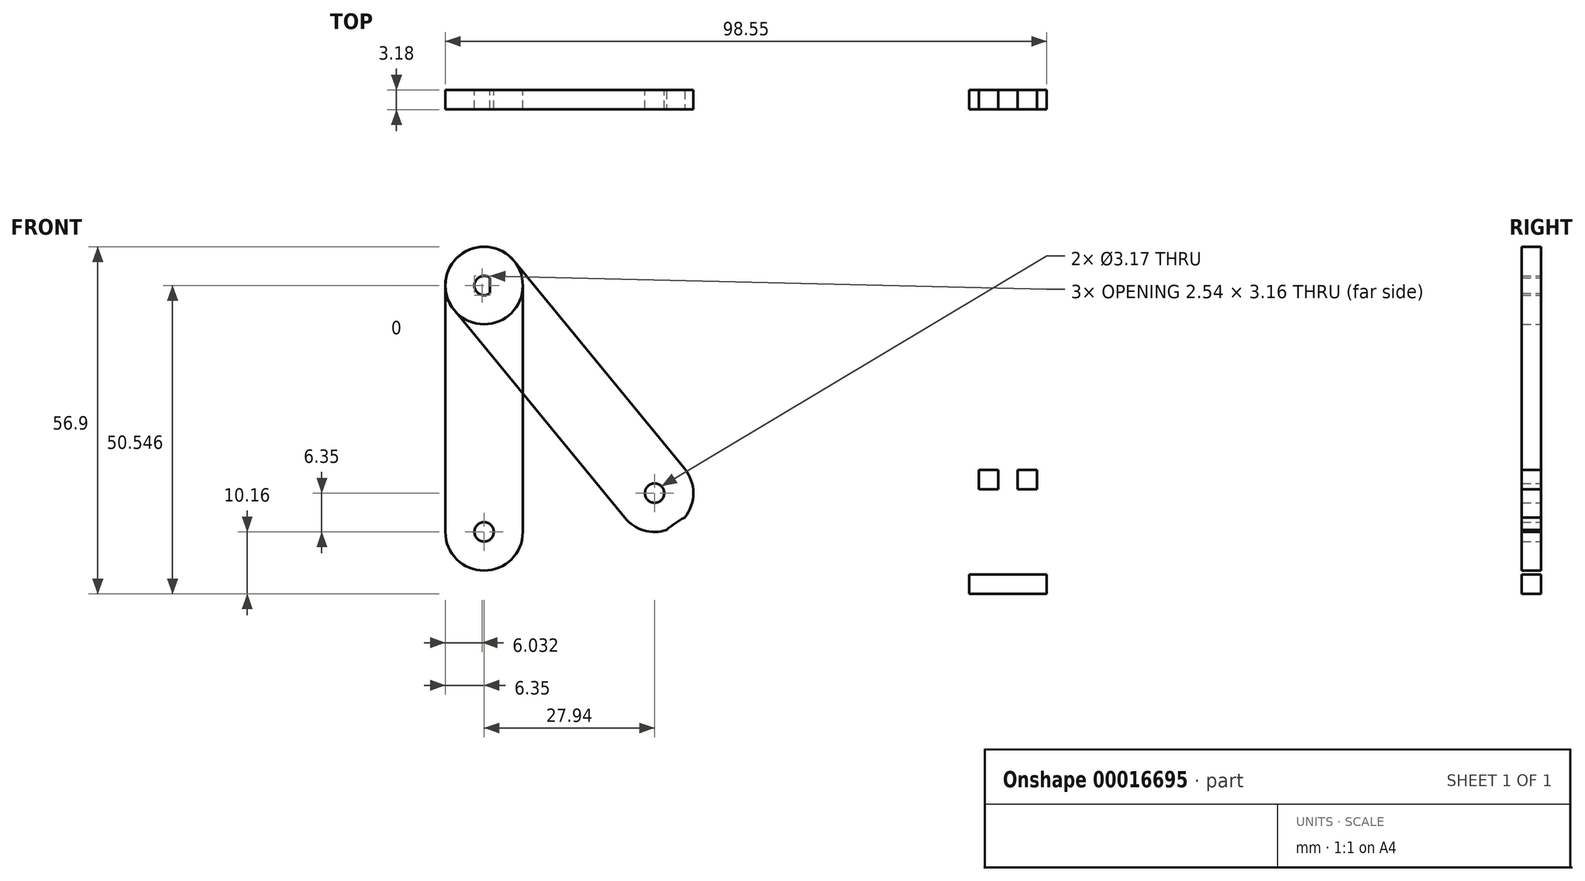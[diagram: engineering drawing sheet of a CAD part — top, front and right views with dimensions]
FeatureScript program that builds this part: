
annotation { "Feature Type Name" : "Feature", "Feature Type Description" : "" }
export const myFeature = defineFeature(function(context is Context, id is Id, definition is map)
    precondition{}
    {
        {
            var Q0;
            Q0=qCreatedBy(makeId("Front.planeOp"),FACE);
            var sketch = newSketch(context, id + "F0", { "sketchPlane" : qUnion([Q0])});
            skLineSegment(sketch, "E0.bottom", {"start": v(6.35, 0) * mm, "end": v(98.55, 0) * mm});
            skLineSegment(sketch, "E0.left", {"start": v(0, 6.35) * mm, "end": v(0, 13.97) * mm});
            skLineSegment(sketch, "E0.right", {"start": v(98.55, 0) * mm, "end": v(98.55, 20.32) * mm});
            skLineSegment(sketch, "E1.top", {"start": v(96.96, 17.15) * mm, "end": v(93.79, 17.15) * mm});
            skLineSegment(sketch, "E1.left", {"start": v(96.96, 20.32) * mm, "end": v(96.96, 17.15) * mm});
            skLineSegment(sketch, "E1.right", {"start": v(93.79, 20.32) * mm, "end": v(93.79, 17.15) * mm});
            skLineSegment(sketch, "E2.top", {"start": v(90.61, 17.15) * mm, "end": v(87.44, 17.15) * mm});
            skLineSegment(sketch, "E2.left", {"start": v(90.61, 20.32) * mm, "end": v(90.61, 17.15) * mm});
            skLineSegment(sketch, "E2.right", {"start": v(87.44, 20.32) * mm, "end": v(87.44, 17.15) * mm});
            skLineSegment(sketch, "E3.bottom", {"start": v(98.55, 20.32) * mm, "end": v(85.85, 20.32) * mm});
            skLineSegment(sketch, "E3.left", {"start": v(98.55, 20.32) * mm, "end": v(98.55, 17.15) * mm});
            skLineSegment(sketch, "E3.right", {"start": v(85.85, 20.32) * mm, "end": v(85.85, 17.15) * mm});
            skLineSegment(sketch, "E4", {"start": v(98.55, 10.16) * mm, "end": v(0, 10.16) * mm, "construction": true});
            skLineSegment(sketch, "E5", {"start": v(85.85, 20.32) * mm, "end": v(6.35, 20.32) * mm});
            skLineSegment(sketch, "E6", {"start": v(85.85, 17.15) * mm, "end": v(87.44, 17.15) * mm});
            skLineSegment(sketch, "E7", {"start": v(98.55, 17.14) * mm, "end": v(96.96, 17.14) * mm});
            skLineSegment(sketch, "E8", {"start": v(93.79, 17.15) * mm, "end": v(90.61, 17.15) * mm});
            skLineSegment(sketch, "E9.0.MirrorCS", {"start": v(85.85, 0) * mm, "end": v(85.85, 3.18) * mm});
            skLineSegment(sketch, "E10.0.MirrorCS", {"start": v(87.44, 0) * mm, "end": v(87.44, 3.18) * mm});
            skLineSegment(sketch, "E11.0.MirrorCS", {"start": v(85.85, 3.18) * mm, "end": v(87.44, 3.18) * mm});
            skLineSegment(sketch, "E12.0.MirrorCS", {"start": v(98.55, 0) * mm, "end": v(85.85, 0) * mm});
            skLineSegment(sketch, "E13.0.MirrorCS", {"start": v(90.61, 0) * mm, "end": v(90.61, 3.18) * mm});
            skLineSegment(sketch, "E14.0.MirrorCS", {"start": v(90.61, 3.18) * mm, "end": v(87.44, 3.18) * mm});
            skLineSegment(sketch, "E15.0.MirrorCS", {"start": v(93.79, 3.18) * mm, "end": v(90.61, 3.18) * mm});
            skLineSegment(sketch, "E16.0.MirrorCS", {"start": v(93.79, 0) * mm, "end": v(93.79, 3.18) * mm});
            skLineSegment(sketch, "E17.0.MirrorCS", {"start": v(96.96, 3.18) * mm, "end": v(93.79, 3.18) * mm});
            skLineSegment(sketch, "E18.0.MirrorCS", {"start": v(96.96, 0) * mm, "end": v(96.96, 3.18) * mm});
            skLineSegment(sketch, "E19.0.MirrorCS", {"start": v(98.55, 3.18) * mm, "end": v(96.96, 3.18) * mm});
            skCircle(sketch, "E20", {"center": v(34.3, 16.51) * mm, "radius": 1.59 * mm});
            skCircle(sketch, "E21", {"center": v(6.35, 10.16) * mm, "radius": 1.59 * mm});
            skPoint(sketch, "E22.visualSharp", {"position": v(0, 20.32) * mm});
            skArc(sketch, "E22.filletArc", {"start": v(6.35, 20.32) * mm, "mid": v(1.86, 18.46) * mm, "end": v(0, 13.97) * mm});
            skPoint(sketch, "E23.visualSharp", {"position": v(0, 0) * mm});
            skArc(sketch, "E23.filletArc", {"start": v(0, 6.35) * mm, "mid": v(1.86, 1.86) * mm, "end": v(6.35, 0) * mm});
            skLineSegment(sketch, "E24", {"start": v(6.35, 13.97) * mm, "end": v(6.35, 6.35) * mm, "construction": true});
            skPoint(sketch, "E25", {"position": v(92.2, 10.16) * mm});
            skPoint(sketch, "E26", {"position": v(52.07, 10.16) * mm});
            skPoint(sketch, "E27", {"position": v(6.35, 48.52) * mm});
            skLineSegment(sketch, "E28", {"start": v(6.35, 48.52) * mm, "end": v(6.35, 10.16) * mm, "construction": true});
            skLineSegment(sketch, "E29", {"start": v(6.35, 48.52) * mm, "end": v(52.07, 10.16) * mm, "construction": true});
            skSolve(sketch);
        }
        {
            var Q0;
            Q0=makeQuery(id+"F0.imprint","IMPRINT",FACE,{"disambiguationData":[TD([[makeQuery(id+"F0.imprint","IMPRINT",EDGE,{"derivedFrom":sQuery(id+"F0.wireOp",EDGE,"E0.bottom")}),1.0]])]});
            var Q1;
            Q1=makeQuery(id+"F0.imprint","IMPRINT",FACE,{"disambiguationData":[TD([[makeQuery(id+"F0.imprint","IMPRINT",EDGE,{"derivedFrom":sQuery(id+"F0.wireOp",EDGE,"E1.top")}),-1.0]])]});
            var Q2;
            Q2=makeQuery(id+"F0.imprint","IMPRINT",FACE,{"disambiguationData":[TD([[makeQuery(id+"F0.imprint","IMPRINT",EDGE,{"derivedFrom":sQuery(id+"F0.wireOp",EDGE,"E2.top")}),-1.0]])]});
            var Q3;
            {var subQ2=sQuery(id+"F0.wireOp",EDGE,"E10.0.MirrorCS");Q3=makeQuery(id+"F0.imprint","IMPRINT",FACE,{"disambiguationData":[TD([[makeQuery(id+"F0.imprint","IMPRINT",EDGE,{"derivedFrom":subQ2}),-1.0]])]});}
            var Q4;
            {var subQ1=sQuery(id+"F0.wireOp",EDGE,"E16.0.MirrorCS");Q4=makeQuery(id+"F0.imprint","IMPRINT",FACE,{"disambiguationData":[TD([[makeQuery(id+"F0.imprint","IMPRINT",EDGE,{"derivedFrom":subQ1}),-1.0]])]});}
            extrude(context, id + "F1", {"entities" : qUnion([Q0, Q1, Q2, Q3, Q4]), "depth" : 3.17 * mm});
        }
        {
            var Q0;
            Q0=qCreatedBy(makeId("Front.planeOp"),FACE);
            var sketch = newSketch(context, id + "F2", { "sketchPlane" : qUnion([Q0])});
            skCircle(sketch, "E30.0", {"center": v(6.35, 10.16) * mm, "radius": 1.59 * mm});
            skLineSegment(sketch, "E31.bottom", {"start": v(6.35, 3.81) * mm, "end": v(6.35, 3.81) * mm});
            skLineSegment(sketch, "E31.top", {"start": v(6.35, 56.9) * mm, "end": v(6.35, 56.9) * mm});
            skLineSegment(sketch, "E31.left", {"start": v(0, 10.16) * mm, "end": v(0, 50.55) * mm});
            skLineSegment(sketch, "E31.right", {"start": v(12.7, 10.16) * mm, "end": v(12.7, 50.55) * mm});
            skPoint(sketch, "E32.visualSharp", {"position": v(12.7, 3.81) * mm});
            skArc(sketch, "E32.filletArc", {"start": v(6.35, 3.81) * mm, "mid": v(10.84, 5.67) * mm, "end": v(12.7, 10.16) * mm});
            skPoint(sketch, "E33.visualSharp", {"position": v(0, 3.81) * mm});
            skArc(sketch, "E33.filletArc", {"start": v(0, 10.16) * mm, "mid": v(1.86, 5.67) * mm, "end": v(6.35, 3.81) * mm});
            skPoint(sketch, "E34.visualSharp", {"position": v(12.7, 56.9) * mm});
            skArc(sketch, "E34.filletArc", {"start": v(12.7, 50.55) * mm, "mid": v(10.84, 55.04) * mm, "end": v(6.35, 56.9) * mm});
            skPoint(sketch, "E35.visualSharp", {"position": v(0, 56.9) * mm});
            skArc(sketch, "E35.filletArc", {"start": v(6.35, 56.9) * mm, "mid": v(1.86, 55.04) * mm, "end": v(0, 50.55) * mm});
            skArc(sketch, "E36", {"start": v(7.3, 51.82) * mm, "mid": v(4.76, 50.55) * mm, "end": v(7.3, 49.28) * mm});
            skLineSegment(sketch, "E37", {"start": v(7.3, 51.82) * mm, "end": v(7.3, 49.28) * mm});
            skSolve(sketch);
        }
        {
            var Q0;
            Q0=makeQuery(id+"F2.imprint","IMPRINT",FACE,{"disambiguationData":[TD([[makeQuery(id+"F2.imprint","IMPRINT",EDGE,{"derivedFrom":sQuery(id+"F2.wireOp",EDGE,"E30.0")}),-1.0]])]});
            extrude(context, id + "F3", {"entities" : qUnion([Q0]), "depth" : 3.17 * mm});
        }
        {
            var Q0;
            Q0=qCreatedBy(makeId("Front.planeOp"),FACE);
            var sketch = newSketch(context, id + "F4", { "sketchPlane" : qUnion([Q0])});
            skCircle(sketch, "E38.0", {"center": v(34.3, 16.51) * mm, "radius": 1.59 * mm});
            skArc(sketch, "E39", {"start": v(11.26, 54.58) * mm, "mid": v(2.32, 55.45) * mm, "end": v(1.44, 46.52) * mm});
            skArc(sketch, "E40", {"start": v(29.38, 12.48) * mm, "mid": v(38.32, 11.6) * mm, "end": v(39.2, 20.54) * mm});
            skLineSegment(sketch, "E41", {"start": v(1.44, 46.52) * mm, "end": v(29.38, 12.48) * mm});
            skLineSegment(sketch, "E42", {"start": v(39.2, 20.54) * mm, "end": v(11.26, 54.58) * mm});
            skArc(sketch, "E43.0", {"start": v(7.3, 51.82) * mm, "mid": v(4.76, 50.55) * mm, "end": v(7.3, 49.28) * mm});
            skLineSegment(sketch, "E44.0", {"start": v(7.3, 51.82) * mm, "end": v(7.3, 49.28) * mm});
            skSolve(sketch);
        }
        {
            var Q0;
            Q0=makeQuery(id+"F4.imprint","IMPRINT",FACE,{"disambiguationData":[TD([[makeQuery(id+"F4.imprint","IMPRINT",EDGE,{"derivedFrom":sQuery(id+"F4.wireOp",EDGE,"E38.0")}),-1.0]])]});
            extrude(context, id + "F5", {"entities" : qUnion([Q0]), "depth" : 3.17 * mm});
        }
        {
            var Q0;
            Q0=qCreatedBy(makeId("Front.planeOp"),FACE);
            var sketch = newSketch(context, id + "F6", { "sketchPlane" : qUnion([Q0])});
            skCircle(sketch, "E45", {"center": v(6.35, 50.55) * mm, "radius": 6.35 * mm});
            skArc(sketch, "E46.0", {"start": v(7.3, 51.82) * mm, "mid": v(4.76, 50.55) * mm, "end": v(7.3, 49.28) * mm});
            skLineSegment(sketch, "E47.0", {"start": v(7.3, 51.82) * mm, "end": v(7.3, 49.28) * mm});
            skSolve(sketch);
        }
        {
            var Q0;
            Q0=makeQuery(id+"F6.imprint","IMPRINT",FACE,{"disambiguationData":[TD([[makeQuery(id+"F6.imprint","IMPRINT",EDGE,{"derivedFrom":sQuery(id+"F6.wireOp",EDGE,"E45")}),1.0]])]});
            extrude(context, id + "F7", {"entities" : qUnion([Q0]), "depth" : 3.17 * mm});
        }
        {
            var Q0;
            Q0=makeQuery(id+"F1.opExtrude","CAP_FACE",FACE,{"disambiguationData":[OSD([sQuery(id+"F0.wireOp",EDGE,"E0.bottom"),sQuery(id+"F0.wireOp",EDGE,"E0.left"),sQuery(id+"F0.wireOp",EDGE,"E0.right"),sQuery(id+"F0.wireOp",EDGE,"E1.left"),sQuery(id+"F0.wireOp",EDGE,"E1.right"),sQuery(id+"F0.wireOp",EDGE,"E2.left"),sQuery(id+"F0.wireOp",EDGE,"E2.right"),sQuery(id+"F0.wireOp",EDGE,"E3.bottom"),sQuery(id+"F0.wireOp",EDGE,"E3.right"),sQuery(id+"F0.wireOp",EDGE,"E5"),sQuery(id+"F0.wireOp",EDGE,"E6"),sQuery(id+"F0.wireOp",EDGE,"E7"),sQuery(id+"F0.wireOp",EDGE,"E8"),sQuery(id+"F0.wireOp",EDGE,"E9.0.MirrorCS"),sQuery(id+"F0.wireOp",EDGE,"E10.0.MirrorCS"),sQuery(id+"F0.wireOp",EDGE,"E11.0.MirrorCS"),sQuery(id+"F0.wireOp",EDGE,"E12.0.MirrorCS"),sQuery(id+"F0.wireOp",EDGE,"E13.0.MirrorCS"),sQuery(id+"F0.wireOp",EDGE,"E15.0.MirrorCS"),sQuery(id+"F0.wireOp",EDGE,"E16.0.MirrorCS"),sQuery(id+"F0.wireOp",EDGE,"E18.0.MirrorCS"),sQuery(id+"F0.wireOp",EDGE,"E19.0.MirrorCS"),sQuery(id+"F0.wireOp",EDGE,"E20"),sQuery(id+"F0.wireOp",EDGE,"E21"),sQuery(id+"F0.wireOp",EDGE,"E22.filletArc"),sQuery(id+"F0.wireOp",EDGE,"E23.filletArc")])],"isStart":false});
            var sketch = newSketch(context, id + "F8", { "sketchPlane" : qUnion([Q0])});
            skCircle(sketch, "E48", {"center": v(45.39, 0.28) * mm, "radius": 13.7 * mm});
            skPoint(sketch, "E49", {"position": v(6.35, -3.17) * mm});
            skLineSegment(sketch, "E50", {"start": v(6.35, -3.17) * mm, "end": v(66.81, -3.17) * mm, "construction": true});
            skLineSegment(sketch, "E51", {"start": v(34.46, 8.52) * mm, "end": v(28.03, 0) * mm});
            skLineSegment(sketch, "E52", {"start": v(56.32, 8.52) * mm, "end": v(62.75, 0) * mm});
            skPoint(sketch, "E53", {"position": v(45.39, 0) * mm});
            skLineSegment(sketch, "E54", {"start": v(28.03, 0) * mm, "end": v(62.75, 0) * mm});
            skSolve(sketch);
        }
        {
            var Q0;
            {var subQ0=sQuery(id+"F8.wireOp",EDGE,"E54");var subQ1=sQuery(id+"F8.wireOp",EDGE,"E48");var subQ3=makeQuery(id+"F8.imprint","INTERSECT",VERTEX,{"disambiguationData":[OD(0.0)],"derivedFrom":[subQ1,subQ0]});var subQ6=sQuery(id+"F8.wireOp",EDGE,"E51");var subQ7=makeQuery(id+"F8.imprint","INTERSECT",VERTEX,{"derivedFrom":[subQ1,subQ6]});var subQ9=sQuery(id+"F8.wireOp",EDGE,"E52");Q0=qUnion([makeQuery(id+"F8.imprint","IMPRINT",FACE,{"disambiguationData":[TD([[makeQuery(id+"F8.imprint","IMPRINT",EDGE,{"disambiguationData":[TD([[subQ3,-1.0]])],"derivedFrom":subQ1}),1.0]])]}),makeQuery(id+"F8.imprint","IMPRINT",FACE,{"disambiguationData":[TD([[makeQuery(id+"F8.imprint","IMPRINT",EDGE,{"derivedFrom":subQ6}),1.0]])]}),makeQuery(id+"F8.imprint","IMPRINT",FACE,{"disambiguationData":[TD([[makeQuery(id+"F8.imprint","IMPRINT",EDGE,{"derivedFrom":subQ9}),-1.0]])]}),makeQuery(id+"F8.imprint","IMPRINT",FACE,{"disambiguationData":[TD([[makeQuery(id+"F8.imprint","IMPRINT",EDGE,{"disambiguationData":[TD([[subQ7,1.0]])],"derivedFrom":subQ1}),1.0]])]})]);}
            extrude(context, id + "F9", {"entities" : qUnion([Q0]), "operationType" : NewBodyOperationType.REMOVE, "oppositeDirection" : true, "depth" : 25.4 * mm});
        }
    });
